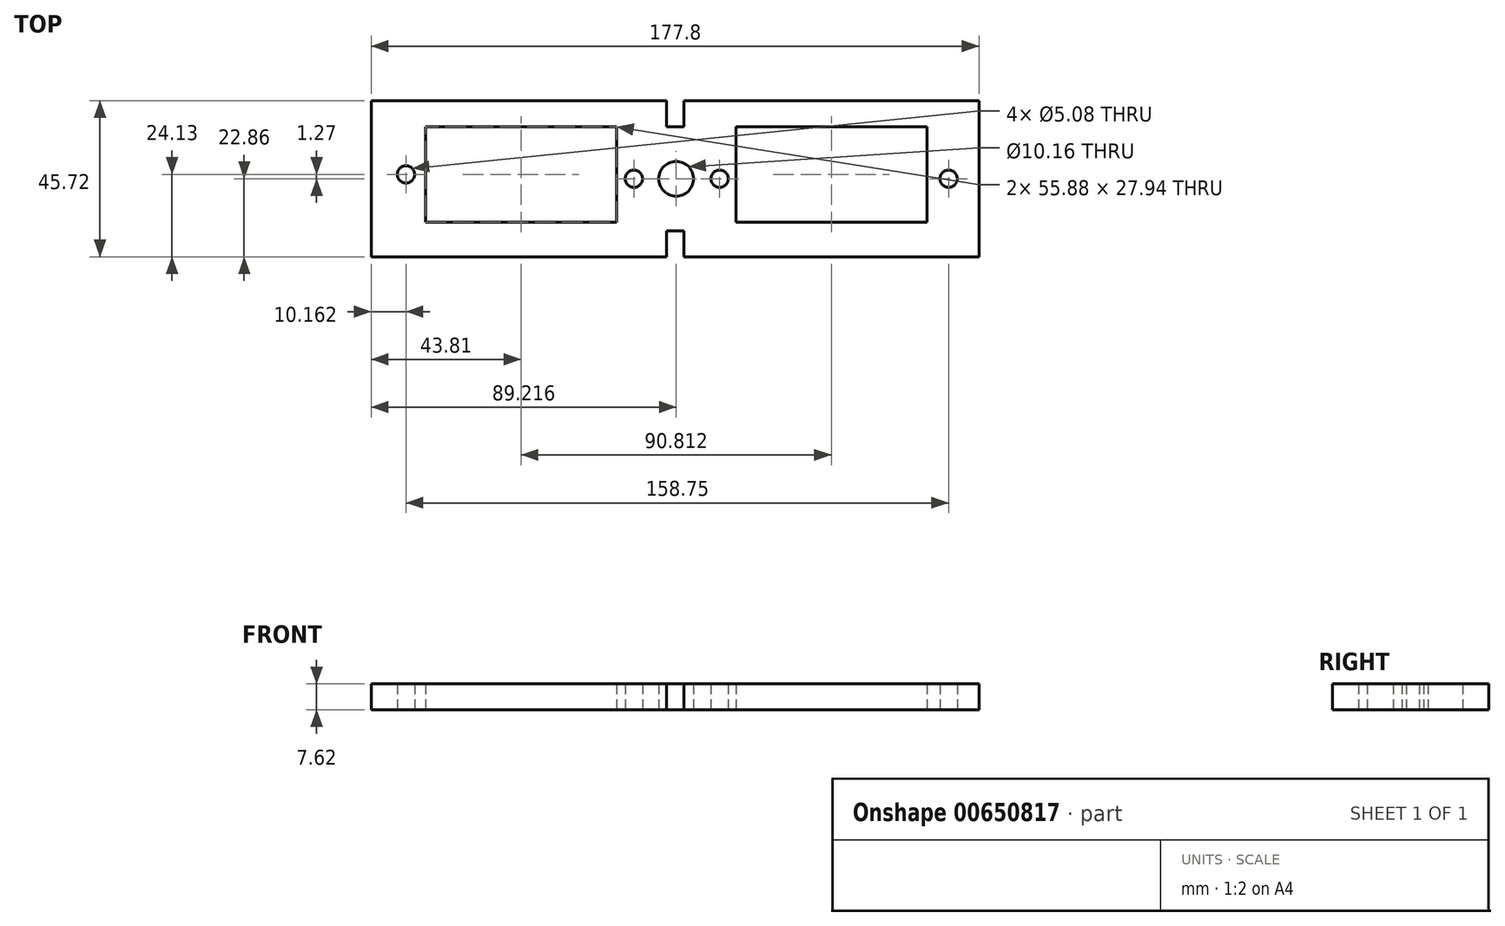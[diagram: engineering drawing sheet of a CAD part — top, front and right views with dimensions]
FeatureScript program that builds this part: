
annotation { "Feature Type Name" : "Feature", "Feature Type Description" : "" }
export const myFeature = defineFeature(function(context is Context, id is Id, definition is map)
    precondition{}
    {
        {
            var Q0;
            Q0=qCreatedBy(makeId("Top.planeOp"),FACE);
            var sketch = newSketch(context, id + "F0", { "sketchPlane" : qUnion([Q0])});
            skLineSegment(sketch, "E0", {"start": v(-86.99, 7.62) * mm, "end": v(-86.99, -38.1) * mm});
            skLineSegment(sketch, "E1", {"start": v(-86.99, -38.1) * mm, "end": v(-0.63, -38.1) * mm});
            skLineSegment(sketch, "E2", {"start": v(-0.63, -38.1) * mm, "end": v(-0.63, -30.48) * mm});
            skLineSegment(sketch, "E3", {"start": v(-0.63, -30.48) * mm, "end": v(4.45, -30.48) * mm});
            skLineSegment(sketch, "E4", {"start": v(4.45, -30.48) * mm, "end": v(4.45, -38.1) * mm});
            skLineSegment(sketch, "E5", {"start": v(4.45, -38.1) * mm, "end": v(90.81, -38.1) * mm});
            skLineSegment(sketch, "E6", {"start": v(90.81, -38.1) * mm, "end": v(90.81, 7.62) * mm});
            skLineSegment(sketch, "E7", {"start": v(90.81, 7.62) * mm, "end": v(4.45, 7.62) * mm});
            skLineSegment(sketch, "E8", {"start": v(4.45, 7.62) * mm, "end": v(4.45, 0) * mm});
            skLineSegment(sketch, "E9", {"start": v(4.45, 0) * mm, "end": v(-0.63, 0) * mm});
            skLineSegment(sketch, "E10", {"start": v(-0.63, 0) * mm, "end": v(-0.63, 7.62) * mm});
            skLineSegment(sketch, "E11", {"start": v(-0.63, 7.62) * mm, "end": v(-86.99, 7.62) * mm});
            skLineSegment(sketch, "E12", {"start": v(19.7, 0) * mm, "end": v(19.7, -27.94) * mm});
            skLineSegment(sketch, "E13", {"start": v(19.7, -27.94) * mm, "end": v(75.57, -27.94) * mm});
            skLineSegment(sketch, "E14", {"start": v(75.57, -27.94) * mm, "end": v(75.57, 0) * mm});
            skLineSegment(sketch, "E15", {"start": v(75.57, 0) * mm, "end": v(19.7, 0) * mm});
            skLineSegment(sketch, "E16", {"start": v(-15.24, 0) * mm, "end": v(-15.24, -27.94) * mm});
            skLineSegment(sketch, "E17", {"start": v(-15.24, -27.94) * mm, "end": v(-71.12, -27.94) * mm});
            skLineSegment(sketch, "E18", {"start": v(-71.12, -27.94) * mm, "end": v(-71.12, 0) * mm});
            skLineSegment(sketch, "E19", {"start": v(-71.12, 0) * mm, "end": v(-15.24, 0) * mm});
            skCircle(sketch, "E20", {"center": v(2.23, -15.24) * mm, "radius": 5.08 * mm});
            skCircle(sketch, "E21", {"center": v(81.92, -15.24) * mm, "radius": 2.54 * mm});
            skPoint(sketch, "E22.startSnap0", {"position": v(-71.12, -13.97) * mm});
            skCircle(sketch, "E23", {"center": v(-76.83, -13.97) * mm, "radius": 2.54 * mm});
            skCircle(sketch, "E24", {"center": v(-10.16, -15.24) * mm, "radius": 2.54 * mm});
            skCircle(sketch, "E25", {"center": v(14.93, -15.24) * mm, "radius": 2.54 * mm});
            skSolve(sketch);
        }
        {
            var Q0;
            Q0 = qSketchRegion(id + "F0", true);
            extrude(context, id + "F1", {"entities" : qUnion([Q0]), "depth" : 7.62 * mm, "offsetDistance" : 25.4 * mm});
        }
    });
